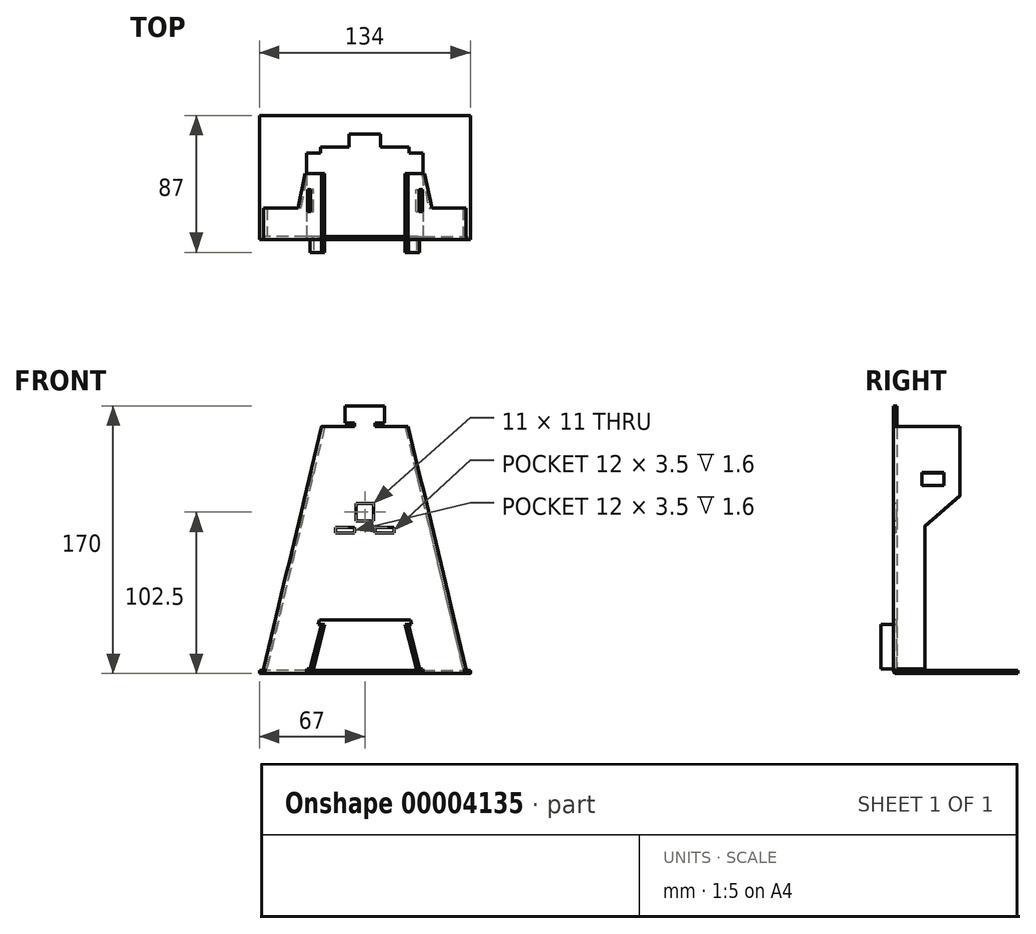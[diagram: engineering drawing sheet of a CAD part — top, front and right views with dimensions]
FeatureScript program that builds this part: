
annotation { "Feature Type Name" : "Feature", "Feature Type Description" : "" }
export const myFeature = defineFeature(function(context is Context, id is Id, definition is map)
    precondition{}
    {
        {
            var Q0;
            Q0=qCreatedBy(makeId("Front.planeOp"),FACE);
            var sketch = newSketch(context, id + "F0", { "sketchPlane" : qUnion([Q0])});
            skLineSegment(sketch, "E0", {"start": v(-67, 0) * mm, "end": v(-37, 0) * mm});
            skLineSegment(sketch, "E1", {"start": v(-6.5, 157) * mm, "end": v(-27.5, 157) * mm});
            skLineSegment(sketch, "E2", {"start": v(-67, 0) * mm, "end": v(-67, 2) * mm});
            skLineSegment(sketch, "E3", {"start": v(-67, 2) * mm, "end": v(-64.5, 2) * mm});
            skLineSegment(sketch, "E4", {"start": v(-64.5, 2) * mm, "end": v(-27.5, 157) * mm});
            skLineSegment(sketch, "E5", {"start": v(-6.5, 157) * mm, "end": v(-6.5, 159) * mm});
            skLineSegment(sketch, "E6", {"start": v(-6.5, 159) * mm, "end": v(-12.5, 159) * mm});
            skLineSegment(sketch, "E7", {"start": v(-12.5, 159) * mm, "end": v(-12.5, 170) * mm});
            skLineSegment(sketch, "E8", {"start": v(-12.5, 170) * mm, "end": v(0, 170) * mm});
            skLineSegment(sketch, "E9", {"start": v(-28.88, 34) * mm, "end": v(0, 34) * mm});
            skLineSegment(sketch, "E10", {"start": v(-37, 0) * mm, "end": v(-37, 2) * mm});
            skLineSegment(sketch, "E11", {"start": v(-37, 2) * mm, "end": v(-64.5, 2) * mm});
            skLineSegment(sketch, "E12", {"start": v(-37, 2) * mm, "end": v(-28.88, 34) * mm});
            skLineSegment(sketch, "E13", {"start": v(-37, 0) * mm, "end": v(0, 0) * mm});
            skLineSegment(sketch, "E14", {"start": v(0, 0) * mm, "end": v(0, 2) * mm});
            skLineSegment(sketch, "E15", {"start": v(0, 2) * mm, "end": v(-37, 2) * mm});
            skLineSegment(sketch, "E16.0.MirrorCS", {"start": v(6.5, 157) * mm, "end": v(6.5, 159) * mm});
            skLineSegment(sketch, "E16.1.MirrorCS", {"start": v(6.5, 159) * mm, "end": v(12.5, 159) * mm});
            skLineSegment(sketch, "E16.2.MirrorCS", {"start": v(67, 2) * mm, "end": v(64.5, 2) * mm});
            skLineSegment(sketch, "E16.3.MirrorCS", {"start": v(12.5, 159) * mm, "end": v(12.5, 170) * mm});
            skLineSegment(sketch, "E16.4.MirrorCS", {"start": v(12.5, 170) * mm, "end": v(0, 170) * mm});
            skLineSegment(sketch, "E16.5.MirrorCS", {"start": v(0, 2) * mm, "end": v(37, 2) * mm});
            skLineSegment(sketch, "E16.6.MirrorCS", {"start": v(37, 2) * mm, "end": v(64.5, 2) * mm});
            skLineSegment(sketch, "E16.7.MirrorCS", {"start": v(37, 0) * mm, "end": v(0, 0) * mm});
            skLineSegment(sketch, "E16.8.MirrorCS", {"start": v(67, 0) * mm, "end": v(37, 0) * mm});
            skLineSegment(sketch, "E16.9.MirrorCS", {"start": v(37, 2) * mm, "end": v(28.88, 34) * mm});
            skLineSegment(sketch, "E16.10.MirrorCS", {"start": v(64.5, 2) * mm, "end": v(27.5, 157) * mm});
            skLineSegment(sketch, "E16.11.MirrorCS", {"start": v(28.88, 34) * mm, "end": v(0, 34) * mm});
            skLineSegment(sketch, "E16.12.MirrorCS", {"start": v(6.5, 157) * mm, "end": v(27.5, 157) * mm});
            skLineSegment(sketch, "E17", {"start": v(67, 0) * mm, "end": v(67, 2) * mm});
            skLineSegment(sketch, "E18", {"start": v(37, 2) * mm, "end": v(37, 0) * mm});
            skLineSegment(sketch, "E19.rect.bottom", {"start": v(5.5, 97) * mm, "end": v(-5.5, 97) * mm});
            skLineSegment(sketch, "E19.rect.top", {"start": v(5.5, 108) * mm, "end": v(-5.5, 108) * mm});
            skLineSegment(sketch, "E19.rect.left", {"start": v(5.5, 97) * mm, "end": v(5.5, 108) * mm});
            skLineSegment(sketch, "E19.rect.right", {"start": v(-5.5, 97) * mm, "end": v(-5.5, 108) * mm});
            skPoint(sketch, "E19.rect.middle", {"position": v(0, 102.5) * mm});
            skLineSegment(sketch, "E20", {"start": v(-29.62, 31.1) * mm, "end": v(-27.62, 31.1) * mm});
            skLineSegment(sketch, "E21", {"start": v(-27.62, 31.1) * mm, "end": v(-25.62, 31.1) * mm});
            skLineSegment(sketch, "E22", {"start": v(-27.62, 31.1) * mm, "end": v(-34.75, 2.97) * mm});
            skLineSegment(sketch, "E23", {"start": v(-25.62, 31.1) * mm, "end": v(-32.75, 2.98) * mm});
            skLineSegment(sketch, "E24", {"start": v(-32.75, 2.98) * mm, "end": v(-34.75, 2.97) * mm});
            skLineSegment(sketch, "E25", {"start": v(-34.75, 2.97) * mm, "end": v(-36.75, 2.97) * mm});
            skLineSegment(sketch, "E26.0.MirrorCS", {"start": v(32.75, 2.98) * mm, "end": v(34.75, 2.97) * mm});
            skLineSegment(sketch, "E26.1.MirrorCS", {"start": v(34.75, 2.97) * mm, "end": v(36.75, 2.97) * mm});
            skLineSegment(sketch, "E26.2.MirrorCS", {"start": v(27.62, 31.1) * mm, "end": v(34.75, 2.97) * mm});
            skLineSegment(sketch, "E26.3.MirrorCS", {"start": v(25.62, 31.1) * mm, "end": v(32.75, 2.98) * mm});
            skLineSegment(sketch, "E26.4.MirrorCS", {"start": v(29.62, 31.1) * mm, "end": v(27.62, 31.1) * mm});
            skLineSegment(sketch, "E26.5.MirrorCS", {"start": v(27.62, 31.1) * mm, "end": v(25.62, 31.1) * mm});
            skSolve(sketch);
        }
        {
            var Q0;
            Q0=makeQuery(id+"F0.imprint","IMPRINT",FACE,{"disambiguationData":[TD([[makeQuery(id+"F0.imprint","IMPRINT",EDGE,{"derivedFrom":sQuery(id+"F0.wireOp",EDGE,"E1")}),1.0]])]});
            var Q1;
            {var subQ1=sQuery(id+"F0.wireOp",EDGE,"a8b98979-38b8-43c3-a65a-645619267603");Q1=makeQuery(id+"F0.imprint","IMPRINT",FACE,{"disambiguationData":[TD([[makeQuery(id+"F0.imprint","IMPRINT",EDGE,{"derivedFrom":subQ1}),-1.0]])]});}
            var Q2;
            Q2=makeQuery(id+"F0.imprint","IMPRINT",FACE,{"disambiguationData":[TD([[makeQuery(id+"F0.imprint","IMPRINT",EDGE,{"derivedFrom":sQuery(id+"F0.wireOp",EDGE,"54274c23-2078-45d5-885f-e596e8b6fb5a")}),1.0]])]});
            var Q3;
            Q3=makeQuery(id+"F0.imprint","IMPRINT",FACE,{"disambiguationData":[TD([[makeQuery(id+"F0.imprint","IMPRINT",EDGE,{"derivedFrom":sQuery(id+"F0.wireOp",EDGE,"ea0e8ca1-e0de-4e66-b8e3-257bfb28e4e0")}),-1.0]])]});
            var Q4;
            {var subQ1=sQuery(id+"F0.wireOp",EDGE,"E20");Q4=makeQuery(id+"F0.imprint","IMPRINT",FACE,{"disambiguationData":[TD([[makeQuery(id+"F0.imprint","IMPRINT",EDGE,{"derivedFrom":subQ1}),-1.0]])]});}
            var Q5;
            Q5=makeQuery(id+"F0.imprint","IMPRINT",FACE,{"disambiguationData":[TD([[makeQuery(id+"F0.imprint","IMPRINT",EDGE,{"derivedFrom":sQuery(id+"F0.wireOp",EDGE,"E21")}),-1.0]])]});
            var Q6;
            Q6=makeQuery(id+"F0.imprint","IMPRINT",FACE,{"disambiguationData":[TD([[makeQuery(id+"F0.imprint","IMPRINT",EDGE,{"derivedFrom":sQuery(id+"F0.wireOp",EDGE,"E26.0.MirrorCS")}),1.0]])]});
            var Q7;
            {var subQ1=sQuery(id+"F0.wireOp",EDGE,"E26.1.MirrorCS");Q7=makeQuery(id+"F0.imprint","IMPRINT",FACE,{"disambiguationData":[TD([[makeQuery(id+"F0.imprint","IMPRINT",EDGE,{"derivedFrom":subQ1}),1.0]])]});}
            extrude(context, id + "F1", {"entities" : qUnion([Q0, Q1, Q2, Q3, Q4, Q5, Q6, Q7]), "oppositeDirection" : true, "depth" : 2 * mm});
        }
        {
            var Q0;
            Q0=makeQuery(id+"F0.imprint","IMPRINT",FACE,{"disambiguationData":[TD([[makeQuery(id+"F0.imprint","IMPRINT",EDGE,{"derivedFrom":sQuery(id+"F0.wireOp",EDGE,"E0")}),1.0]])]});
            var Q1;
            Q1=makeQuery(id+"F0.imprint","IMPRINT",FACE,{"disambiguationData":[TD([[makeQuery(id+"F0.imprint","IMPRINT",EDGE,{"derivedFrom":sQuery(id+"F0.wireOp",EDGE,"E16.2.MirrorCS")}),1.0]])]});
            var Q2;
            Q2=makeQuery(id+"F0.imprint","IMPRINT",FACE,{"disambiguationData":[TD([[makeQuery(id+"F0.imprint","IMPRINT",EDGE,{"derivedFrom":sQuery(id+"F0.wireOp",EDGE,"E10")}),-1.0]])]});
            var Q3;
            Q3=makeQuery(id+"F0.imprint","IMPRINT",FACE,{"disambiguationData":[TD([[makeQuery(id+"F0.imprint","IMPRINT",EDGE,{"derivedFrom":sQuery(id+"F0.wireOp",EDGE,"E14")}),-1.0]])]});
            extrude(context, id + "F2", {"entities" : qUnion([Q0, Q1, Q2, Q3]), "operationType" : NewBodyOperationType.ADD, "oppositeDirection" : true, "depth" : 79 * mm});
        }
        {
            var Q0;
            Q0=makeQuery(id+"F2.opExtrude","SWEPT_FACE",FACE,{"disambiguationData":[OSD([sQuery(id+"F0.wireOp",EDGE,"E3"),sQuery(id+"F0.wireOp",EDGE,"E11"),sQuery(id+"F0.wireOp",EDGE,"E15"),sQuery(id+"F0.wireOp",EDGE,"E16.2.MirrorCS"),sQuery(id+"F0.wireOp",EDGE,"E16.5.MirrorCS"),sQuery(id+"F0.wireOp",EDGE,"E16.6.MirrorCS")])]});
            var sketch = newSketch(context, id + "F3", { "sketchPlane" : qUnion([Q0])});
            skLineSegment(sketch, "E27", {"start": v(0, 67) * mm, "end": v(-10, 67) * mm});
            skLineSegment(sketch, "E28", {"start": v(-10, 67) * mm, "end": v(-10, 59) * mm});
            skLineSegment(sketch, "E29", {"start": v(-10, 59) * mm, "end": v(-28, 59) * mm});
            skLineSegment(sketch, "E30", {"start": v(-28, 59) * mm, "end": v(-28, 55) * mm});
            skLineSegment(sketch, "E31", {"start": v(-28, 55) * mm, "end": v(-37, 55) * mm});
            skLineSegment(sketch, "E32", {"start": v(-37, 55) * mm, "end": v(-37, 0) * mm});
            skLineSegment(sketch, "E33.0.MirrorCS", {"start": v(0, 67) * mm, "end": v(10, 67) * mm});
            skLineSegment(sketch, "E33.1.MirrorCS", {"start": v(10, 67) * mm, "end": v(10, 59) * mm});
            skLineSegment(sketch, "E33.2.MirrorCS", {"start": v(10, 59) * mm, "end": v(28, 59) * mm});
            skLineSegment(sketch, "E33.3.MirrorCS", {"start": v(28, 59) * mm, "end": v(28, 55) * mm});
            skLineSegment(sketch, "E33.4.MirrorCS", {"start": v(37, 55) * mm, "end": v(37, 0) * mm});
            skLineSegment(sketch, "E33.5.MirrorCS", {"start": v(28, 55) * mm, "end": v(37, 55) * mm});
            skSolve(sketch);
        }
        {
            var Q0;
            Q0=makeQuery(id+"F3.imprint","IMPRINT",FACE,{"disambiguationData":[TD([[makeQuery(id+"F3.imprint","IMPRINT",EDGE,{"derivedFrom":sQuery(id+"F3.wireOp",EDGE,"E27")}),1.0]])]});
            extrude(context, id + "F4", {"entities" : qUnion([Q0]), "operationType" : NewBodyOperationType.REMOVE, "endBound" : BoundingType.UP_TO_NEXT, "oppositeDirection" : true, "depth" : 25 * mm});
        }
        {
            var Q0;
            Q0=makeQuery(id+"F1.opExtrude","CAP_FACE",FACE,{"disambiguationData":[OSD([sQuery(id+"F0.wireOp",EDGE,"E1"),sQuery(id+"F0.wireOp",EDGE,"E4"),sQuery(id+"F0.wireOp",EDGE,"E5"),sQuery(id+"F0.wireOp",EDGE,"E6"),sQuery(id+"F0.wireOp",EDGE,"E7"),sQuery(id+"F0.wireOp",EDGE,"E8"),sQuery(id+"F0.wireOp",EDGE,"E9"),sQuery(id+"F0.wireOp",EDGE,"E11"),sQuery(id+"F0.wireOp",EDGE,"E12"),sQuery(id+"F0.wireOp",EDGE,"E16.0.MirrorCS"),sQuery(id+"F0.wireOp",EDGE,"E16.1.MirrorCS"),sQuery(id+"F0.wireOp",EDGE,"E16.3.MirrorCS"),sQuery(id+"F0.wireOp",EDGE,"E16.4.MirrorCS"),sQuery(id+"F0.wireOp",EDGE,"E16.6.MirrorCS"),sQuery(id+"F0.wireOp",EDGE,"E16.9.MirrorCS"),sQuery(id+"F0.wireOp",EDGE,"E16.10.MirrorCS"),sQuery(id+"F0.wireOp",EDGE,"E16.11.MirrorCS"),sQuery(id+"F0.wireOp",EDGE,"E16.12.MirrorCS"),sQuery(id+"F0.wireOp",EDGE,"E19.rect.bottom"),sQuery(id+"F0.wireOp",EDGE,"E19.rect.top"),sQuery(id+"F0.wireOp",EDGE,"E19.rect.left"),sQuery(id+"F0.wireOp",EDGE,"E19.rect.right"),sQuery(id+"F0.wireOp",EDGE,"E20"),sQuery(id+"F0.wireOp",EDGE,"E21"),sQuery(id+"F0.wireOp",EDGE,"E23"),sQuery(id+"F0.wireOp",EDGE,"E24"),sQuery(id+"F0.wireOp",EDGE,"E25"),sQuery(id+"F0.wireOp",EDGE,"E26.0.MirrorCS"),sQuery(id+"F0.wireOp",EDGE,"E26.1.MirrorCS"),sQuery(id+"F0.wireOp",EDGE,"E26.3.MirrorCS"),sQuery(id+"F0.wireOp",EDGE,"E26.4.MirrorCS"),sQuery(id+"F0.wireOp",EDGE,"E26.5.MirrorCS")])],"isStart":false});
            var sketch = newSketch(context, id + "F5", { "sketchPlane" : qUnion([Q0])});
            skLineSegment(sketch, "E34", {"start": v(-27.5, 157) * mm, "end": v(-25.55, 156.54) * mm});
            skLineSegment(sketch, "E35", {"start": v(-64.3, 2.83) * mm, "end": v(-27.5, 157) * mm});
            skLineSegment(sketch, "E36", {"start": v(-25.55, 156.54) * mm, "end": v(-62.25, 2.83) * mm});
            skLineSegment(sketch, "E37", {"start": v(-62.25, 2.83) * mm, "end": v(-64.3, 2.83) * mm});
            skLineSegment(sketch, "E38.0.MirrorCS", {"start": v(62.25, 2.83) * mm, "end": v(64.3, 2.83) * mm});
            skLineSegment(sketch, "E38.1.MirrorCS", {"start": v(27.5, 157) * mm, "end": v(25.55, 156.54) * mm});
            skLineSegment(sketch, "E38.2.MirrorCS", {"start": v(25.55, 156.54) * mm, "end": v(62.25, 2.83) * mm});
            skLineSegment(sketch, "E38.3.MirrorCS", {"start": v(64.3, 2.83) * mm, "end": v(27.5, 157) * mm});
            skSolve(sketch);
        }
        {
            var Q0;
            Q0=makeQuery(id+"F5.imprint","IMPRINT",FACE,{"disambiguationData":[TD([[makeQuery(id+"F5.imprint","IMPRINT",EDGE,{"derivedFrom":sQuery(id+"F5.wireOp",EDGE,"E34")}),-1.0]])]});
            var Q1;
            Q1=makeQuery(id+"F5.imprint","IMPRINT",FACE,{"disambiguationData":[TD([[makeQuery(id+"F5.imprint","IMPRINT",EDGE,{"derivedFrom":sQuery(id+"F5.wireOp",EDGE,"E38.0.MirrorCS")}),1.0]])]});
            extrude(context, id + "F6", {"entities" : qUnion([Q0, Q1]), "operationType" : NewBodyOperationType.ADD, "depth" : 40 * mm});
        }
        {
            var Q0;
            Q0=makeQuery(id+"F6.boolean.opBoolean","MERGE",FACE,{"derivedFrom":[makeQuery(id+"F1.opExtrude","SWEPT_FACE",FACE,{"disambiguationData":[OSD([sQuery(id+"F0.wireOp",EDGE,"E16.10.MirrorCS")])]}),makeQuery(id+"F6.opExtrude","SWEPT_FACE",FACE,{"disambiguationData":[OSD([sQuery(id+"F5.wireOp",EDGE,"E35")])]})]});
            var sketch = newSketch(context, id + "F7", { "sketchPlane" : qUnion([Q0])});
            skLineSegment(sketch, "E39", {"start": v(42, 101.32) * mm, "end": v(20, 81.32) * mm});
            skLineSegment(sketch, "E40", {"start": v(20, 81.32) * mm, "end": v(20, -12.18) * mm});
            skLineSegment(sketch, "E41", {"start": v(20, -12.18) * mm, "end": v(42, -12.18) * mm});
            skLineSegment(sketch, "E42", {"start": v(42, -12.18) * mm, "end": v(42, 101.32) * mm});
            skLineSegment(sketch, "E43.bottom", {"start": v(18, 116.32) * mm, "end": v(32, 116.32) * mm});
            skLineSegment(sketch, "E43.top", {"start": v(18, 107.72) * mm, "end": v(32, 107.72) * mm});
            skLineSegment(sketch, "E43.left", {"start": v(18, 116.32) * mm, "end": v(18, 107.72) * mm});
            skLineSegment(sketch, "E43.right", {"start": v(32, 116.32) * mm, "end": v(32, 107.72) * mm});
            skSolve(sketch);
        }
        {
            var Q0;
            Q0=makeQuery(id+"F7.imprint","IMPRINT",FACE,{"disambiguationData":[TD([[makeQuery(id+"F7.imprint","IMPRINT",EDGE,{"derivedFrom":sQuery(id+"F7.wireOp",EDGE,"E43.bottom")}),-1.0]])]});
            var Q1;
            Q1=makeQuery(id+"F7.imprint","IMPRINT",FACE,{"disambiguationData":[TD([[makeQuery(id+"F7.imprint","IMPRINT",EDGE,{"derivedFrom":sQuery(id+"F7.wireOp",EDGE,"E39")}),1.0]])]});
            extrude(context, id + "F8", {"entities" : qUnion([Q0, Q1]), "operationType" : NewBodyOperationType.REMOVE, "endBound" : BoundingType.UP_TO_NEXT, "oppositeDirection" : true, "depth" : 25 * mm});
        }
        {
            var Q0;
            Q0=makeQuery(id+"F6.boolean.opBoolean","MERGE",FACE,{"derivedFrom":[makeQuery(id+"F1.opExtrude","SWEPT_FACE",FACE,{"disambiguationData":[OSD([sQuery(id+"F0.wireOp",EDGE,"E4")])]}),makeQuery(id+"F6.opExtrude","SWEPT_FACE",FACE,{"disambiguationData":[OSD([sQuery(id+"F5.wireOp",EDGE,"E38.3.MirrorCS")])]})]});
            var sketch = newSketch(context, id + "F9", { "sketchPlane" : qUnion([Q0])});
            skLineSegment(sketch, "E44", {"start": v(-42, 101.32) * mm, "end": v(-20, 81.32) * mm});
            skLineSegment(sketch, "E45", {"start": v(-20, 81.32) * mm, "end": v(-20, -12.18) * mm});
            skLineSegment(sketch, "E46", {"start": v(-20, -12.18) * mm, "end": v(-42, -12.18) * mm});
            skLineSegment(sketch, "E47", {"start": v(-42, -12.18) * mm, "end": v(-42, 101.32) * mm});
            skLineSegment(sketch, "E48.bottom", {"start": v(-32, 116.32) * mm, "end": v(-18, 116.32) * mm});
            skLineSegment(sketch, "E48.top", {"start": v(-32, 107.72) * mm, "end": v(-18, 107.72) * mm});
            skLineSegment(sketch, "E48.left", {"start": v(-32, 116.32) * mm, "end": v(-32, 107.72) * mm});
            skLineSegment(sketch, "E48.right", {"start": v(-18, 116.32) * mm, "end": v(-18, 107.72) * mm});
            skSolve(sketch);
        }
        {
            var Q0;
            Q0=makeQuery(id+"F9.imprint","IMPRINT",FACE,{"disambiguationData":[TD([[makeQuery(id+"F9.imprint","IMPRINT",EDGE,{"derivedFrom":sQuery(id+"F9.wireOp",EDGE,"E44")}),-1.0]])]});
            var Q1;
            Q1=makeQuery(id+"F9.imprint","IMPRINT",FACE,{"disambiguationData":[TD([[makeQuery(id+"F9.imprint","IMPRINT",EDGE,{"derivedFrom":sQuery(id+"F9.wireOp",EDGE,"E48.bottom")}),-1.0]])]});
            extrude(context, id + "F10", {"entities" : qUnion([Q0, Q1]), "operationType" : NewBodyOperationType.REMOVE, "endBound" : BoundingType.UP_TO_NEXT, "oppositeDirection" : true, "depth" : 25 * mm});
        }
        {
            var Q0;
            Q0=makeQuery(id+"F0.imprint","IMPRINT",FACE,{"disambiguationData":[TD([[makeQuery(id+"F0.imprint","IMPRINT",EDGE,{"derivedFrom":sQuery(id+"F0.wireOp",EDGE,"E1")}),1.0]])]});
            var sketch = newSketch(context, id + "F11", { "sketchPlane" : qUnion([Q0])});
            skLineSegment(sketch, "E49.bottom", {"start": v(-18.5, 92.7) * mm, "end": v(-6.5, 92.7) * mm});
            skLineSegment(sketch, "E49.top", {"start": v(-18.5, 89.2) * mm, "end": v(-6.5, 89.2) * mm});
            skLineSegment(sketch, "E49.left", {"start": v(-18.5, 92.7) * mm, "end": v(-18.5, 89.2) * mm});
            skLineSegment(sketch, "E49.right", {"start": v(-6.5, 92.7) * mm, "end": v(-6.5, 89.2) * mm});
            skLineSegment(sketch, "E50.0.MirrorCS", {"start": v(6.5, 92.7) * mm, "end": v(6.5, 89.2) * mm});
            skLineSegment(sketch, "E50.1.MirrorCS", {"start": v(18.5, 89.2) * mm, "end": v(6.5, 89.2) * mm});
            skLineSegment(sketch, "E50.2.MirrorCS", {"start": v(18.5, 92.7) * mm, "end": v(6.5, 92.7) * mm});
            skLineSegment(sketch, "E50.3.MirrorCS", {"start": v(18.5, 92.7) * mm, "end": v(18.5, 89.2) * mm});
            skSolve(sketch);
        }
        {
            var Q0;
            Q0=makeQuery(id+"F11.imprint","IMPRINT",FACE,{"disambiguationData":[TD([[makeQuery(id+"F11.imprint","IMPRINT",EDGE,{"derivedFrom":sQuery(id+"F11.wireOp",EDGE,"E49.bottom")}),-1.0]])]});
            var Q1;
            Q1=makeQuery(id+"F11.imprint","IMPRINT",FACE,{"disambiguationData":[TD([[makeQuery(id+"F11.imprint","IMPRINT",EDGE,{"derivedFrom":sQuery(id+"F11.wireOp",EDGE,"E50.0.MirrorCS")}),1.0]])]});
            extrude(context, id + "F12", {"entities" : qUnion([Q0, Q1]), "operationType" : NewBodyOperationType.REMOVE, "oppositeDirection" : true, "depth" : 1.6 * mm});
        }
        {
            var Q0;
            Q0=makeQuery(id+"F0.imprint","IMPRINT",FACE,{"disambiguationData":[TD([[makeQuery(id+"F0.imprint","IMPRINT",EDGE,{"derivedFrom":sQuery(id+"F0.wireOp",EDGE,"E21")}),-1.0]])]});
            var Q1;
            Q1=makeQuery(id+"F0.imprint","IMPRINT",FACE,{"disambiguationData":[TD([[makeQuery(id+"F0.imprint","IMPRINT",EDGE,{"derivedFrom":sQuery(id+"F0.wireOp",EDGE,"E26.0.MirrorCS")}),1.0]])]});
            extrude(context, id + "F13", {"entities" : qUnion([Q0, Q1]), "operationType" : NewBodyOperationType.ADD, "depth" : 8 * mm});
        }
        {
            var Q0;
            Q0=makeQuery(id+"F1.opExtrude","CAP_EDGE",EDGE,{"disambiguationData":[OSD([sQuery(id+"F0.wireOp",EDGE,"E16.10.MirrorCS")])],"isStart":true});
            var Q1;
            Q1=makeQuery(id+"F1.opExtrude","CAP_EDGE",EDGE,{"disambiguationData":[OSD([sQuery(id+"F0.wireOp",EDGE,"E4")])],"isStart":true});
            var Q2;
            Q2=makeQuery(id+"F6.opExtrude","CAP_EDGE",EDGE,{"disambiguationData":[OSD([sQuery(id+"F5.wireOp",EDGE,"E36")])],"isStart":true});
            var Q3;
            Q3=makeQuery(id+"F6.opExtrude","CAP_EDGE",EDGE,{"disambiguationData":[OSD([sQuery(id+"F5.wireOp",EDGE,"E38.2.MirrorCS")])],"isStart":true});
            fillet(context, id + "F14", {"entities" : qUnion([Q0, Q1, Q2, Q3]), "radius" : 2 * mm, "tangentPropagation" : true, "rho" : 0.5, "crossSection" : FilletCrossSection.CONIC, "allowEdgeOverflow" : false});
        }
        {
            var Q0;
            {var subQ0=sQuery(id+"F0.wireOp",EDGE,"E0");var subQ1=sQuery(id+"F0.wireOp",EDGE,"E13");var subQ2=sQuery(id+"F0.wireOp",EDGE,"E16.7.MirrorCS");var subQ3=sQuery(id+"F0.wireOp",EDGE,"E16.8.MirrorCS");var subQ4=sQuery(id+"F0.wireOp",EDGE,"E17");Q0=makeQuery(id+"F4.boolean.opBoolean","SPLIT",EDGE,{"disambiguationData":[TD([makeQuery(id+"F2.opExtrude","SWEPT_FACE",FACE,{"disambiguationData":[OSD([subQ4])]})])],"derivedFrom":makeQuery(id+"F2.opExtrude","CAP_EDGE",EDGE,{"disambiguationData":[OSD([subQ0,subQ1,subQ2,subQ3])],"isStart":true})});}
            var Q1;
            {var subQ0=sQuery(id+"F0.wireOp",EDGE,"E0");var subQ1=sQuery(id+"F0.wireOp",EDGE,"E13");var subQ2=sQuery(id+"F0.wireOp",EDGE,"E16.7.MirrorCS");var subQ3=sQuery(id+"F0.wireOp",EDGE,"E16.8.MirrorCS");var subQ4=sQuery(id+"F0.wireOp",EDGE,"E2");Q1=makeQuery(id+"F4.boolean.opBoolean","SPLIT",EDGE,{"disambiguationData":[TD([makeQuery(id+"F2.opExtrude","SWEPT_FACE",FACE,{"disambiguationData":[OSD([subQ4])]})])],"derivedFrom":makeQuery(id+"F2.opExtrude","CAP_EDGE",EDGE,{"disambiguationData":[OSD([subQ0,subQ1,subQ2,subQ3])],"isStart":true})});}
            fillet(context, id + "F15", {"entities" : qUnion([Q0, Q1]), "radius" : 1.8 * mm, "tangentPropagation" : true, "rho" : 0.5, "crossSection" : FilletCrossSection.CONIC, "allowEdgeOverflow" : false});
        }
        {
            var Q0;
            Q0=makeQuery(id+"F13.opExtrude","CAP_EDGE",EDGE,{"disambiguationData":[OSD([sQuery(id+"F0.wireOp",EDGE,"E22")])],"isStart":true});
            var Q1;
            Q1=makeQuery(id+"F1.opExtrude","CAP_EDGE",EDGE,{"disambiguationData":[OSD([sQuery(id+"F0.wireOp",EDGE,"E23")])],"isStart":false});
            var Q2;
            Q2=makeQuery(id+"F13.opExtrude","CAP_EDGE",EDGE,{"disambiguationData":[OSD([sQuery(id+"F0.wireOp",EDGE,"E26.2.MirrorCS")])],"isStart":true});
            var Q3;
            Q3=makeQuery(id+"F1.opExtrude","CAP_EDGE",EDGE,{"disambiguationData":[OSD([sQuery(id+"F0.wireOp",EDGE,"E26.3.MirrorCS")])],"isStart":false});
            fillet(context, id + "F16", {"entities" : qUnion([Q0, Q1, Q2, Q3]), "radius" : 1 * mm, "tangentPropagation" : true, "rho" : 0.5, "crossSection" : FilletCrossSection.CONIC, "allowEdgeOverflow" : false});
        }
    });
